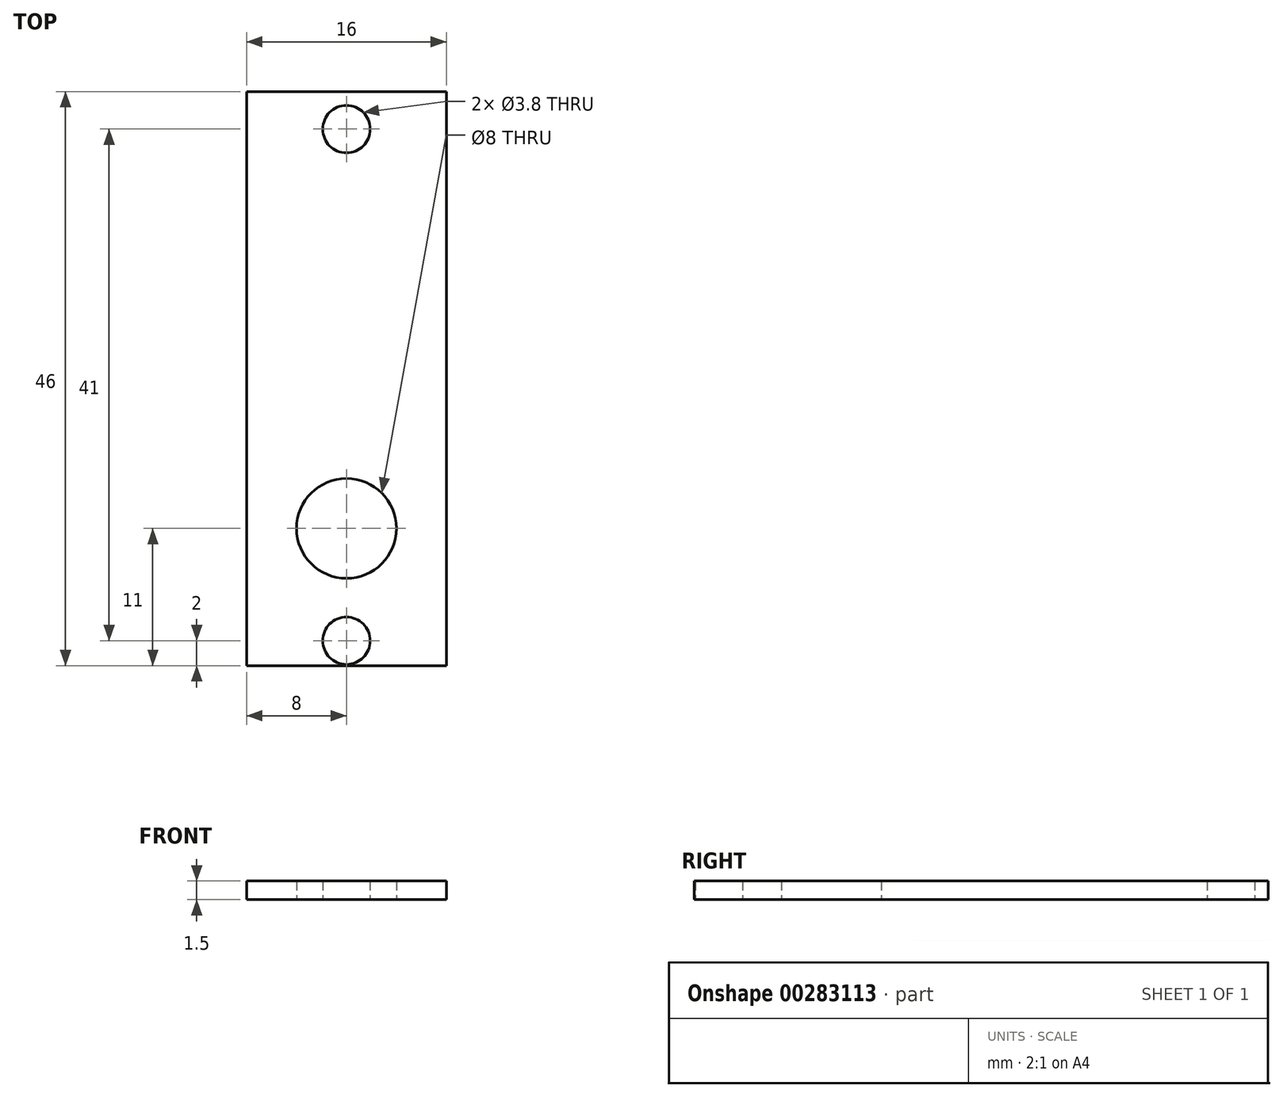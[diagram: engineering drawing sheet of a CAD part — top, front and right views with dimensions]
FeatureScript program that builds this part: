
annotation { "Feature Type Name" : "Feature", "Feature Type Description" : "" }
export const myFeature = defineFeature(function(context is Context, id is Id, definition is map)
    precondition{}
    {
        {
            var Q0;
            Q0=qCreatedBy(makeId("Top.planeOp"),FACE);
            var sketch = newSketch(context, id + "F0", { "sketchPlane" : qUnion([Q0])});
            skLineSegment(sketch, "E0.bottom", {"start": v(-8, 23) * mm, "end": v(8, 23) * mm});
            skLineSegment(sketch, "E0.top", {"start": v(-8, -23) * mm, "end": v(8, -23) * mm});
            skLineSegment(sketch, "E0.left", {"start": v(-8, 23) * mm, "end": v(-8, -23) * mm});
            skLineSegment(sketch, "E0.right", {"start": v(8, 23) * mm, "end": v(8, -23) * mm});
            skPoint(sketch, "E0.middle", {"position": v(0, 0) * mm});
            skCircle(sketch, "E1", {"center": v(0, -21) * mm, "radius": 1.9 * mm});
            skCircle(sketch, "E2.0.1.0", {"center": v(0, 20) * mm, "radius": 1.9 * mm});
            skLineSegment(sketch, "E2.direction1", {"start": v(0, -21) * mm, "end": v(25, -21) * mm, "construction": true});
            skLineSegment(sketch, "E2.direction2", {"start": v(0, -21) * mm, "end": v(0, 20) * mm, "construction": true});
            skCircle(sketch, "E3", {"center": v(0, -12) * mm, "radius": 4 * mm});
            skSolve(sketch);
        }
        {
            var Q0;
            Q0=makeQuery(id+"F0.imprint","IMPRINT",FACE,{"disambiguationData":[TD([[makeQuery(id+"F0.imprint","IMPRINT",EDGE,{"derivedFrom":sQuery(id+"F0.wireOp",EDGE,"E0.bottom")}),-1.0]])]});
            extrude(context, id + "F1", {"entities" : qUnion([Q0]), "depth" : 1.5 * mm});
        }
    });
